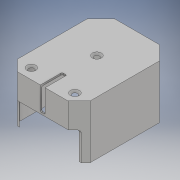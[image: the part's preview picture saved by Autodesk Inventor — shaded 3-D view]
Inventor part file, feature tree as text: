
AUTODESK INVENTOR PART (.ipt)
format: ipt  version: 2017 (Build 210142000, 142)  size: 258,048 bytes
history: native  units: mm
features: extrude x9, sketch x7, other x5, fillet x4, hole x3, projected_geometry x1
ambient origin geometry x8: Origin, YZ Plane, XZ Plane, XY Plane, X Axis, Y Axis, Z Axis, Center Point
bodies: Body1 (feature_tree)
feature tree (29):
  other  "Твердое тело1"
  sketch  "Эскиз1"
  extrude  "Выдавливание1"  Depth=58.6mm
  extrude  "Выдавливание2"  Depth=77.0mm
  fillet  "Сопряжение1"  Radius=11.0mm
  extrude  "Выдавливание3"  Depth=11.0mm
  extrude  "Выдавливание4"  Depth=8.5mm
  extrude  "Выдавливание5"  Depth=8.5mm
  other  "Комбинировать1"
  hole  "Отверстие4"  [1 undecoded]
  hole  "Отверстие5"  [1 undecoded]
  hole  "Отверстие6"  [1 undecoded]
  fillet  "Сопряжение2"  Radius=11.0mm
  fillet  "Сопряжение3"  Radius=1.2mm
  extrude  "Выдавливание6"  Depth=1.5mm TaperAngle=0.0deg
  extrude  "Выдавливание7"  Depth=43.5mm TaperAngle=0.0deg
  extrude  "Выдавливание8"  Depth=1.0mm
  other  "Комбинировать2"
  fillet  "Сопряжение4"  Radius=4.0mm
  extrude  "Выдавливание11"  Depth=17.0mm
  other  "Твердое тело2"
  sketch  "Эскиз2"
  sketch  "Эскиз3"
  sketch  "Эскиз4"
  other  "Твердое тело3"
  sketch  "Эскиз5"
  sketch  "Эскиз6"
  sketch  "Эскиз9"
  projected_geometry  "Спроецированная петля1"
note: 3 required parameter values undecoded (feature->parameter linkage not recoverable at this tier; creation-order binding heuristic only, values carry confidence <= 0.55)
